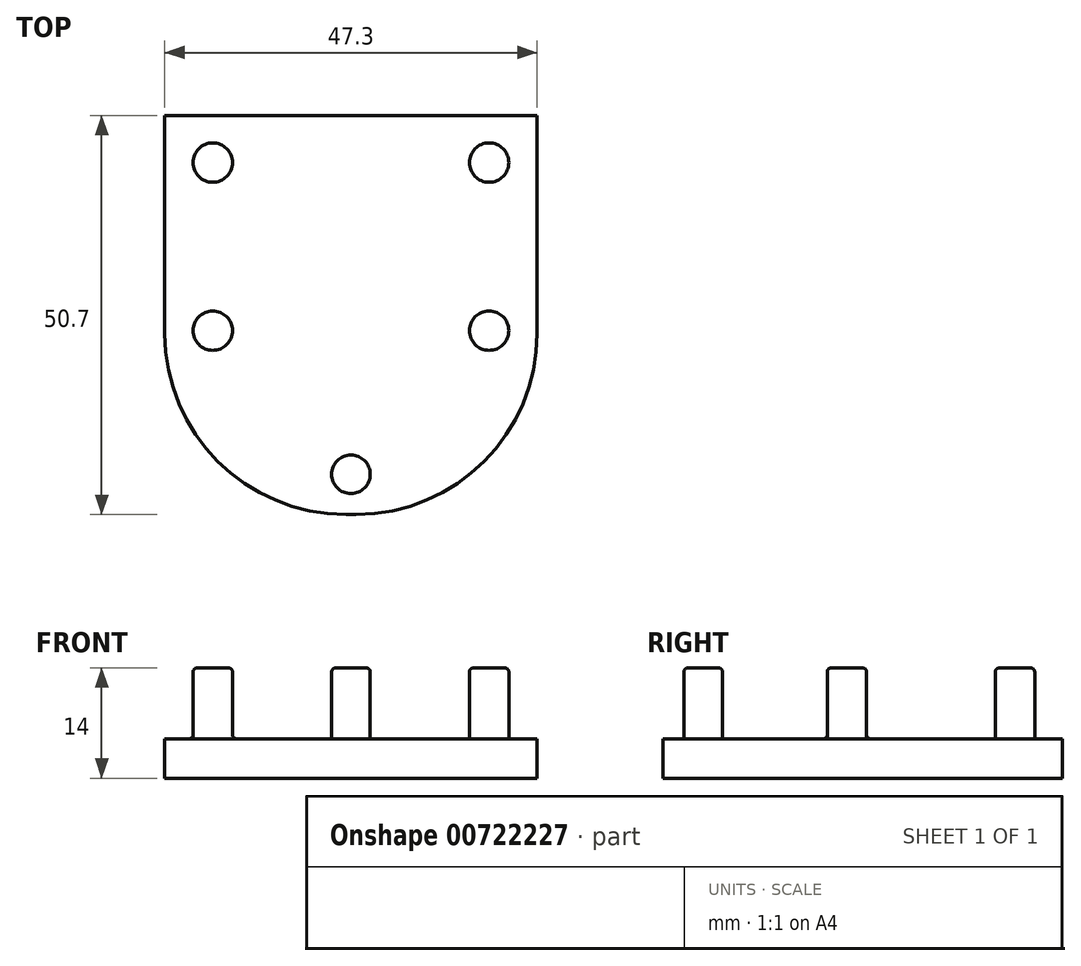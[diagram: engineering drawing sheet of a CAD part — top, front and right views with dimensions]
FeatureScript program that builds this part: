
annotation { "Feature Type Name" : "Feature", "Feature Type Description" : "" }
export const myFeature = defineFeature(function(context is Context, id is Id, definition is map)
    precondition{}
    {
        {
            var Q0;
            Q0=qCreatedBy(makeId("Top.planeOp"),FACE);
            var sketch = newSketch(context, id + "F0", { "sketchPlane" : qUnion([Q0])});
            skLineSegment(sketch, "E0.bottom", {"start": v(-23.65, 25.35) * mm, "end": v(23.65, 25.35) * mm});
            skLineSegment(sketch, "E0.top", {"start": v(-23.65, -25.35) * mm, "end": v(23.65, -25.35) * mm});
            skLineSegment(sketch, "E0.left", {"start": v(-23.65, 25.35) * mm, "end": v(-23.65, -25.35) * mm});
            skLineSegment(sketch, "E0.right", {"start": v(23.65, 25.35) * mm, "end": v(23.65, -25.35) * mm});
            skPoint(sketch, "E0.middle", {"position": v(0, 0) * mm});
            skCircle(sketch, "E1", {"center": v(-17.55, 19.35) * mm, "radius": 2.5 * mm, "construction": true});
            skCircle(sketch, "E2", {"center": v(17.55, 19.35) * mm, "radius": 2.5 * mm, "construction": true});
            skCircle(sketch, "E3", {"center": v(17.55, -2) * mm, "radius": 2.5 * mm, "construction": true});
            skCircle(sketch, "E4", {"center": v(-17.55, -2) * mm, "radius": 2.5 * mm, "construction": true});
            skCircle(sketch, "E5", {"center": v(0, -20.25) * mm, "radius": 2.45 * mm, "construction": true});
            skSolve(sketch);
        }
        {
            var Q0;
            Q0 = qSketchRegion(id + "F0", true);
            extrude(context, id + "F1", {"entities" : qUnion([Q0]), "depth" : 5 * mm, "offsetDistance" : 25 * mm});
        }
        {
            var Q0;
            Q0=makeQuery(id+"F1.opExtrude","SWEPT_EDGE",EDGE,{"disambiguationData":[OSD([sQuery(id+"F0.wireOp",EDGE,"E0.top"),sQuery(id+"F0.wireOp",EDGE,"E0.left")])]});
            var Q1;
            Q1=makeQuery(id+"F1.opExtrude","SWEPT_EDGE",EDGE,{"disambiguationData":[OSD([sQuery(id+"F0.wireOp",EDGE,"E0.top"),sQuery(id+"F0.wireOp",EDGE,"E0.right")])]});
            fillet(context, id + "F2", {"entities" : qUnion([Q0, Q1]), "radius" : 23 * mm, "tangentPropagation" : true, "allowEdgeOverflow" : false});
        }
        {
            var Q0;
            Q0=makeQuery(id+"F1.opExtrude","CAP_FACE",FACE,{"disambiguationData":[OSD([sQuery(id+"F0.wireOp",EDGE,"E0.bottom"),sQuery(id+"F0.wireOp",EDGE,"E0.top"),sQuery(id+"F0.wireOp",EDGE,"E0.left"),sQuery(id+"F0.wireOp",EDGE,"E0.right")])],"isStart":false});
            var sketch = newSketch(context, id + "F3", { "sketchPlane" : qUnion([Q0])});
            skCircle(sketch, "E6.0", {"center": v(-17.55, 19.35) * mm, "radius": 2.5 * mm});
            skCircle(sketch, "E7.0", {"center": v(17.55, 19.35) * mm, "radius": 2.5 * mm});
            skCircle(sketch, "E8.0", {"center": v(17.55, -2) * mm, "radius": 2.5 * mm});
            skCircle(sketch, "E9.0", {"center": v(-17.55, -2) * mm, "radius": 2.5 * mm});
            skCircle(sketch, "E10.0", {"center": v(0, -20.25) * mm, "radius": 2.45 * mm});
            skSolve(sketch);
        }
        {
            var Q0;
            Q0 = qSketchRegion(id + "F3", true);
            extrude(context, id + "F4", {"entities" : qUnion([Q0]), "operationType" : NewBodyOperationType.ADD, "depth" : 9 * mm, "offsetDistance" : 25 * mm});
        }
        {
            var Q0;
            Q0=makeQuery(id+"F4.opExtrude","CAP_EDGE",EDGE,{"disambiguationData":[OSD([sQuery(id+"F3.wireOp",EDGE,"E6.0")])],"isStart":false});
            var Q1;
            Q1=makeQuery(id+"F4.opExtrude","CAP_EDGE",EDGE,{"disambiguationData":[OSD([sQuery(id+"F3.wireOp",EDGE,"E7.0")])],"isStart":false});
            var Q2;
            Q2=makeQuery(id+"F4.opExtrude","CAP_EDGE",EDGE,{"disambiguationData":[OSD([sQuery(id+"F3.wireOp",EDGE,"E8.0")])],"isStart":false});
            var Q3;
            Q3=makeQuery(id+"F4.opExtrude","CAP_EDGE",EDGE,{"disambiguationData":[OSD([sQuery(id+"F3.wireOp",EDGE,"E10.0")])],"isStart":false});
            var Q4;
            Q4=makeQuery(id+"F4.opExtrude","SWEPT_FACE",FACE,{"disambiguationData":[OSD([sQuery(id+"F3.wireOp",EDGE,"E9.0")])]});
            fillet(context, id + "F5", {"entities" : qUnion([Q0, Q1, Q2, Q3, Q4]), "radius" : .5 * mm, "tangentPropagation" : true, "allowEdgeOverflow" : false});
        }
    });
